# Revit family: Rax 150 surface - Generic
name_source: partatom
category: Lighting Fixtures
revit_build: Autodesk Revit Architecture 2014 (Build: 20140709_2115(x64)
units: mm (PartAtom-declared; Revit-internal decimal feet)

## types (1)
- Rax 150 Surface
    Apparent Load = 240 VA
    ArticleNumber = See URL hyperlink
    AssetType = Moveable/Fixed
    BIMObjectName = Rax 150 Surface.rfa
    BSAB 96 = SNB.2
    BallastsCELMAEnergyEfficiencyIndex = Class A1/A2
    CCSClassCode = UAC
    CCSClassName = Belysningsarmatur
    CCSTopnode = L
    Color Filter = 16777215
    Colour = White
    ControlGearPosition = Integrated
    Description = 70-80-35 General Lighting Systems
    Diameter 1 = 173 mm
    Dimming Lamp Color Temperature Shift = <None>
    DocumentReference = See URL hyperlink
    Documentation = See URL hyperlink
    Finish = Powder coated
    Frame = Riegens_Aluminium_Powder coated white gloss 25
    HasProtectiveEarth = TRUE
    Height 1 = 189 mm
    Height 2 = 203 mm
    IP_Code = IP20
    IfcExportAs = IfcLightFixtureType'
    IfcExportType = NOTDEFINED'
    InsulationStandardClass = Class 1
    InternalFuse = Only required in emergency versions
    LampColourRenderingIndex = Ra>80 / Ra>90
    LampRating = 15W / 21W
    LampType = LED
    Light Source Definition (family) = Point+HemiSpherical
    LightFixtureMountingType = Surface
    LightFixturePlacingType = Ceiling
    LightSource = LED 3000K / 4000K
    LuminairePowerFactor = >0,9
    LuminaireType = Recessed Direct, Narrow beam, Asymmetric LED Luminaire
    Manufacturer = Riegens A/S
    ManufacturerURL = www.riegens.com
    Material = Aluminium
    Model = Rax 150 Surface
    ModelReference = Rax 150 Surface
    NominalVoltage = 220-240V
    OmniClass Number = 23.80.70.11
    OmniClass Title = Luminaries for Internal Lighting
    Optic = Plain, white or satin-matt reflector
    Optics = Riegens_Satin-matt
    PhaseReference = IEC recommendations
    Photometric Web File = RaX Surface 150 21W LED 4000K Ra80 Refl. Satinmatt.ies
    PhotometricPerformance = In accordance with BS EN 13032-1
    ProductInformation = http://riegens.co.uk
    Shape = Circle
    Size = Ø173 mm
    Tilt Angle = 90.00°
    TotalWattage = Max. 17W / 23W
    URL = http://riegens.co.uk
    Uniclass 1.4 = JY73
    Uniclass2 = Pr_70_70_49_43 Light-Emitting Diode (LED) Luminaires
    Version = v.1.0

## geometry (parser evidence)
native form markers: Blend x96, Sweep x4
no freeform markers — native parametric forms only
